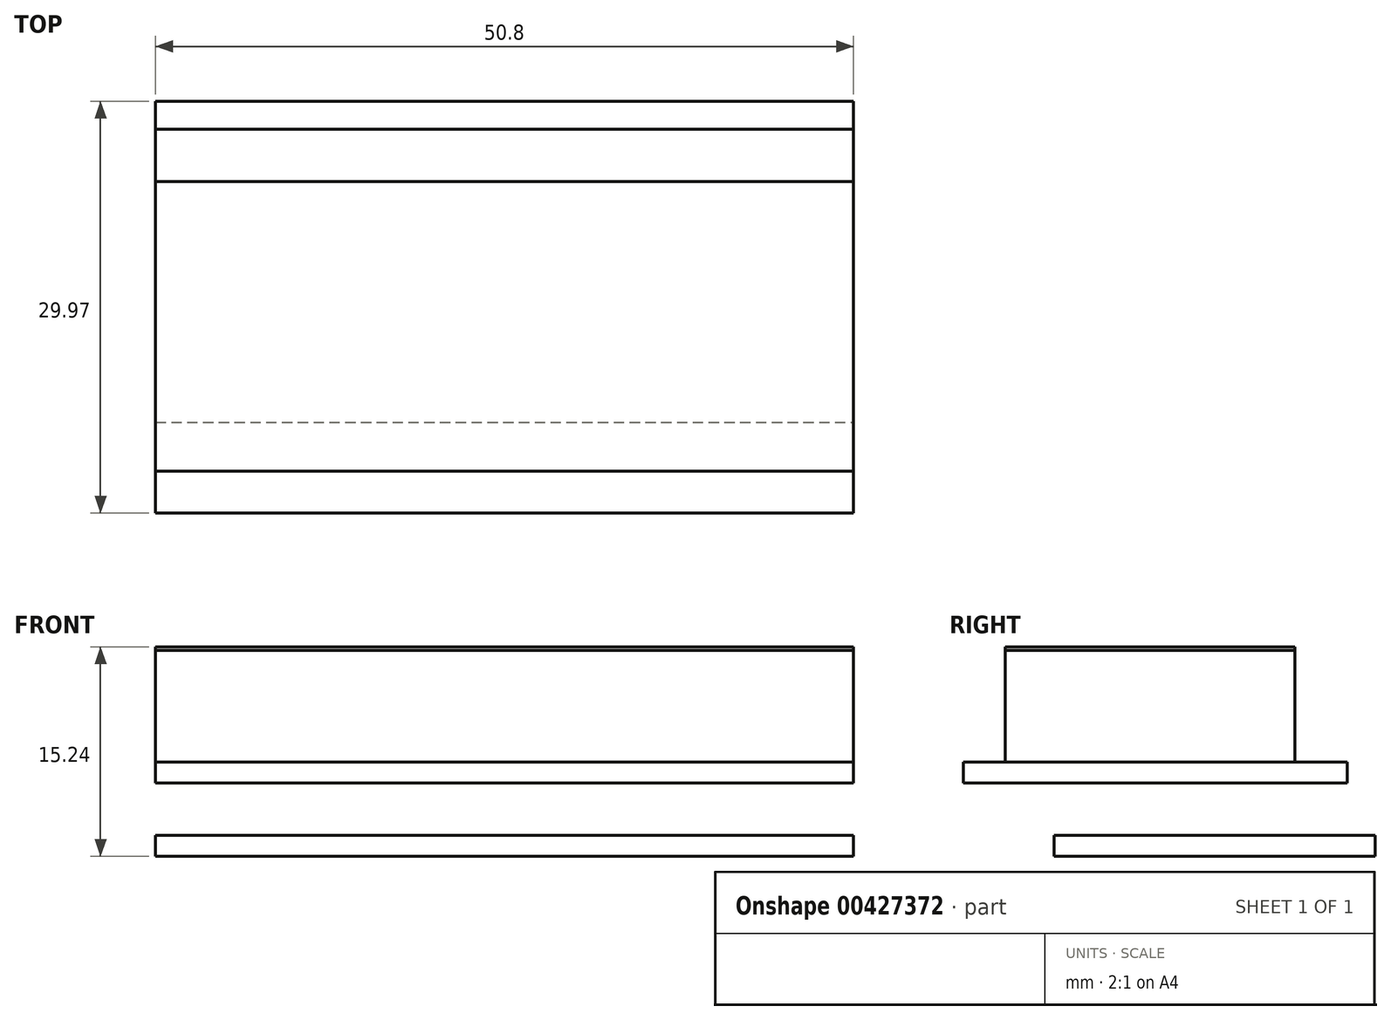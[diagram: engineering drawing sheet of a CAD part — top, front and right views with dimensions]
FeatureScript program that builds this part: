
annotation { "Feature Type Name" : "Feature", "Feature Type Description" : "" }
export const myFeature = defineFeature(function(context is Context, id is Id, definition is map)
    precondition{}
    {
        {
            var Q0;
            Q0=qCreatedBy(makeId("Top.planeOp"),FACE);
            var sketch = newSketch(context, id + "F0", { "sketchPlane" : qUnion([Q0])});
            skLineSegment(sketch, "E0.bottom", {"start": v(0, 0) * mm, "end": v(50.8, 0) * mm});
            skLineSegment(sketch, "E0.top", {"start": v(0, -23.37) * mm, "end": v(50.8, -23.37) * mm});
            skLineSegment(sketch, "E0.left", {"start": v(0, 0) * mm, "end": v(0, -23.37) * mm});
            skLineSegment(sketch, "E0.right", {"start": v(50.8, 0) * mm, "end": v(50.8, -23.37) * mm});
            skSolve(sketch);
        }
        {
            var Q0;
            {var subQ1=sQuery(id+"F0.wireOp",EDGE,"E0.bottom");Q0=makeQuery(id+"F0.imprint","IMPRINT",FACE,{"disambiguationData":[TD([[makeQuery(id+"F0.imprint","IMPRINT",EDGE,{"derivedFrom":subQ1}),-1.0]])]});}
            var Q1;
            {var subQ0=sQuery(id+"F0.wireOp",EDGE,"E0.right");var subQ1=sQuery(id+"F0.wireOp",EDGE,"E0.top");var subQ2=makeQuery(id+"F0.imprint","INTERSECT",VERTEX,{"derivedFrom":[subQ1,subQ0]});Q1=makeQuery(id+"F0.imprint","IMPRINT",FACE,{"disambiguationData":[TD([[makeQuery(id+"F0.imprint","IMPRINT",EDGE,{"disambiguationData":[TD([[subQ2,1.0]])],"derivedFrom":subQ1}),1.0]])]});}
            extrude(context, id + "F1", {"entities" : qUnion([Q0, Q1]), "oppositeDirection" : true, "depth" : 1.52 * mm, "offsetDistance" : 25.4 * mm});
        }
        {
            var Q0;
            {var subQ1=sQuery(id+"F0.wireOp",EDGE,"E0.bottom");Q0=makeQuery(id+"F0.imprint","IMPRINT",FACE,{"disambiguationData":[TD([[makeQuery(id+"F0.imprint","IMPRINT",EDGE,{"derivedFrom":subQ1}),-1.0]])]});}
            cPlane(context, id + "F2", {"entities" : qUnion([Q0]), "cplaneType" : CPlaneType.OFFSET, "offset" : 3.8 * mm, "width" : 152.4 * mm, "height" : 152.4 * mm});
        }
        {
            var Q0;
            Q0=qCreatedBy(id+"F2.planeOp",FACE);
            var sketch = newSketch(context, id + "F3", { "sketchPlane" : qUnion([Q0])});
            skLineSegment(sketch, "E1.bottom", {"start": v(0, -2.03) * mm, "end": v(50.8, -2.03) * mm});
            skLineSegment(sketch, "E1.top", {"start": v(0, -29.97) * mm, "end": v(50.8, -29.97) * mm});
            skLineSegment(sketch, "E1.left", {"start": v(0, -2.03) * mm, "end": v(0, -29.97) * mm});
            skLineSegment(sketch, "E1.right", {"start": v(50.8, -2.03) * mm, "end": v(50.8, -29.97) * mm});
            skSolve(sketch);
        }
        {
            var Q0;
            Q0 = qSketchRegion(id + "F3", true);
            extrude(context, id + "F4", {"entities" : qUnion([Q0]), "depth" : 1.52 * mm, "offsetDistance" : 25.4 * mm});
        }
        {
            var Q0;
            Q0=makeQuery(id+"F4.opExtrude","CAP_FACE",FACE,{"disambiguationData":[OSD([sQuery(id+"F3.wireOp",EDGE,"E1.bottom"),sQuery(id+"F3.wireOp",EDGE,"E1.top"),sQuery(id+"F3.wireOp",EDGE,"E1.left"),sQuery(id+"F3.wireOp",EDGE,"E1.right")])],"isStart":false});
            cPlane(context, id + "F5", {"entities" : qUnion([Q0]), "cplaneType" : CPlaneType.OFFSET, "offset" : 0 * mm, "width" : 152.4 * mm, "height" : 152.4 * mm});
        }
        {
            var Q0;
            Q0=qCreatedBy(id+"F5.planeOp",FACE);
            var sketch = newSketch(context, id + "F6", { "sketchPlane" : qUnion([Q0])});
            skLineSegment(sketch, "E2.bottom", {"start": v(0, -5.84) * mm, "end": v(50.8, -5.84) * mm});
            skLineSegment(sketch, "E2.top", {"start": v(0, -26.92) * mm, "end": v(50.8, -26.92) * mm});
            skLineSegment(sketch, "E2.left", {"start": v(0, -5.84) * mm, "end": v(0, -26.92) * mm});
            skLineSegment(sketch, "E2.right", {"start": v(50.8, -5.84) * mm, "end": v(50.8, -26.92) * mm});
            skSolve(sketch);
        }
        {
            var Q0;
            Q0=makeQuery(id+"F6.imprint","IMPRINT",FACE,{"disambiguationData":[TD([[makeQuery(id+"F6.imprint","IMPRINT",EDGE,{"derivedFrom":sQuery(id+"F6.wireOp",EDGE,"E2.bottom")}),-1.0]])]});
            extrude(context, id + "F7", {"entities" : qUnion([Q0]), "depth" : 8.13 * mm, "offsetDistance" : 25.4 * mm});
        }
        {
            var Q0;
            Q0=makeQuery(id+"F7.opExtrude","CAP_FACE",FACE,{"disambiguationData":[OSD([sQuery(id+"F6.wireOp",EDGE,"E2.bottom"),sQuery(id+"F6.wireOp",EDGE,"E2.top"),sQuery(id+"F6.wireOp",EDGE,"E2.left"),sQuery(id+"F6.wireOp",EDGE,"E2.right")])],"isStart":false});
            var sketch = newSketch(context, id + "F8", { "sketchPlane" : qUnion([Q0])});
            skLineSegment(sketch, "E3.bottom", {"start": v(0, -5.84) * mm, "end": v(50.8, -5.84) * mm});
            skLineSegment(sketch, "E3.top", {"start": v(0, -26.92) * mm, "end": v(50.8, -26.92) * mm});
            skLineSegment(sketch, "E3.left", {"start": v(0, -5.84) * mm, "end": v(0, -26.92) * mm});
            skLineSegment(sketch, "E3.right", {"start": v(50.8, -5.84) * mm, "end": v(50.8, -26.92) * mm});
            skSolve(sketch);
        }
        {
            var Q0;
            Q0 = qSketchRegion(id + "F8", true);
            extrude(context, id + "F9", {"entities" : qUnion([Q0]), "depth" : 0.25 * mm, "offsetDistance" : 25.4 * mm});
        }
    });
